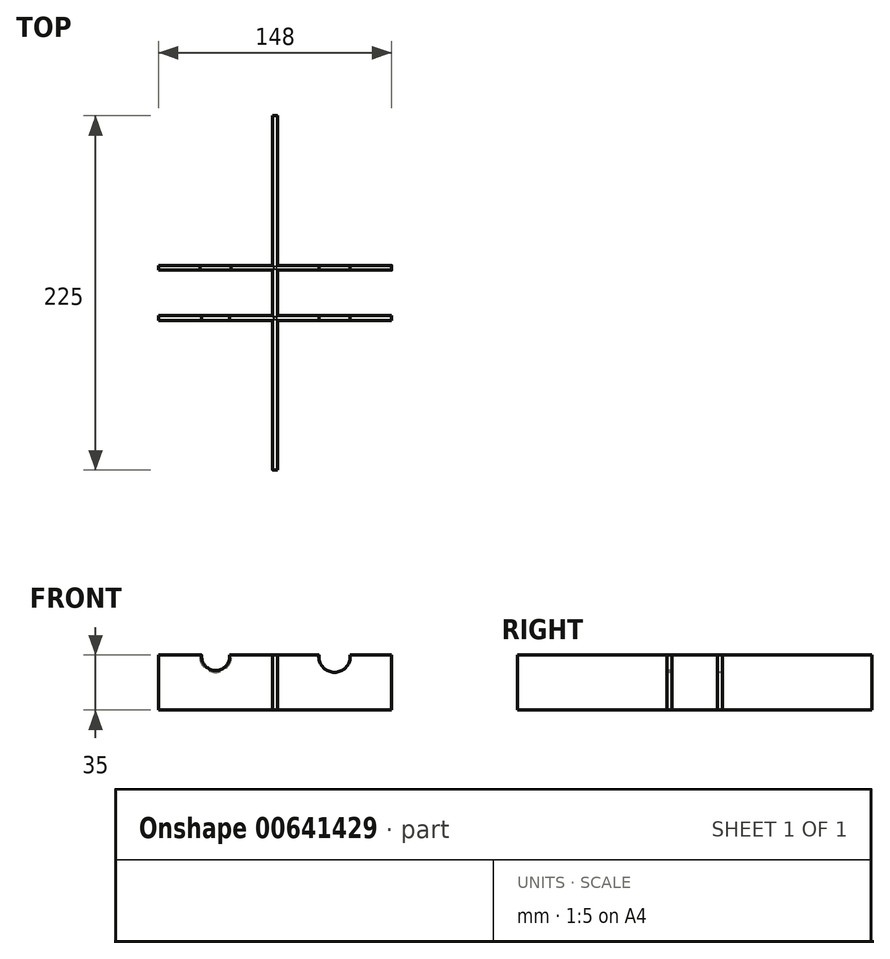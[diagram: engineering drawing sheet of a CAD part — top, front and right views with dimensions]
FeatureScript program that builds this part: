
annotation { "Feature Type Name" : "Feature", "Feature Type Description" : "" }
export const myFeature = defineFeature(function(context is Context, id is Id, definition is map)
    precondition{}
    {
        {
            var Q0;
            Q0=qCreatedBy(makeId("Top.planeOp"),FACE);
            var sketch = newSketch(context, id + "F0", { "sketchPlane" : qUnion([Q0])});
            skPoint(sketch, "E0.middle", {"position": v(0, 0) * mm});
            skLineSegment(sketch, "E1.bottom", {"start": v(1.5, 112.5) * mm, "end": v(-1.5, 112.5) * mm});
            skLineSegment(sketch, "E1.top", {"start": v(1.5, -112.5) * mm, "end": v(-1.5, -112.5) * mm});
            skLineSegment(sketch, "E2", {"start": v(-1.5, -17.5) * mm, "end": v(-74, -17.5) * mm});
            skLineSegment(sketch, "E3", {"start": v(-74, -17.5) * mm, "end": v(-74, -14.5) * mm});
            skLineSegment(sketch, "E4", {"start": v(-74, -14.5) * mm, "end": v(-1.5, -14.5) * mm});
            skLineSegment(sketch, "E5", {"start": v(1.5, -17.5) * mm, "end": v(74, -17.5) * mm});
            skLineSegment(sketch, "E6", {"start": v(74, -17.5) * mm, "end": v(74, -14.5) * mm});
            skLineSegment(sketch, "E7", {"start": v(74, -14.5) * mm, "end": v(1.5, -14.5) * mm});
            skLineSegment(sketch, "E8", {"start": v(-1.5, 14.5) * mm, "end": v(-74, 14.5) * mm});
            skLineSegment(sketch, "E9", {"start": v(-74, 14.5) * mm, "end": v(-74, 17.5) * mm});
            skLineSegment(sketch, "E10", {"start": v(-74, 17.5) * mm, "end": v(-1.5, 17.5) * mm});
            skLineSegment(sketch, "E11", {"start": v(74, 17.5) * mm, "end": v(74, 14.5) * mm});
            skLineSegment(sketch, "E12", {"start": v(74, 17.5) * mm, "end": v(1.5, 17.5) * mm});
            skLineSegment(sketch, "E13", {"start": v(74, 14.5) * mm, "end": v(1.5, 14.5) * mm});
            skLineSegment(sketch, "E14", {"start": v(-1.5, 112.5) * mm, "end": v(-1.5, 17.5) * mm});
            skLineSegment(sketch, "E15", {"start": v(-1.5, 14.5) * mm, "end": v(-1.5, -14.5) * mm});
            skLineSegment(sketch, "E16", {"start": v(-1.5, -17.5) * mm, "end": v(-1.5, -112.5) * mm});
            skLineSegment(sketch, "E17", {"start": v(1.5, 112.5) * mm, "end": v(1.5, 17.5) * mm});
            skLineSegment(sketch, "E18", {"start": v(1.5, 14.5) * mm, "end": v(1.5, -14.5) * mm});
            skLineSegment(sketch, "E19", {"start": v(1.5, -17.5) * mm, "end": v(1.5, -112.5) * mm});
            skSolve(sketch);
        }
        {
            var Q0;
            Q0=makeQuery(id+"F0.imprint","IMPRINT",FACE,{"disambiguationData":[TD([[makeQuery(id+"F0.imprint","IMPRINT",EDGE,{"derivedFrom":sQuery(id+"F0.wireOp",EDGE,"E1.bottom")}),1.0]])]});
            extrude(context, id + "F1", {"entities" : qUnion([Q0]), "depth" : 35 * mm, "offsetDistance" : 25 * mm});
        }
        {
            var Q0;
            Q0=makeQuery(id+"F1.opExtrude","CAP_EDGE",EDGE,{"disambiguationData":[OSD([sQuery(id+"F0.wireOp",EDGE,"E8")])],"isStart":false});
            var Q1;
            Q1=makeQuery(id+"F1.opExtrude","CAP_EDGE",EDGE,{"disambiguationData":[OSD([sQuery(id+"F0.wireOp",EDGE,"E14")])],"isStart":false});
            var Q2;
            Q2=makeQuery(id+"F1.opExtrude","CAP_EDGE",EDGE,{"disambiguationData":[OSD([sQuery(id+"F0.wireOp",EDGE,"E10")])],"isStart":false});
            var Q3;
            Q3=makeQuery(id+"F1.opExtrude","CAP_EDGE",EDGE,{"disambiguationData":[OSD([sQuery(id+"F0.wireOp",EDGE,"E17")])],"isStart":false});
            var Q4;
            Q4=makeQuery(id+"F1.opExtrude","CAP_EDGE",EDGE,{"disambiguationData":[OSD([sQuery(id+"F0.wireOp",EDGE,"E12")])],"isStart":false});
            var Q5;
            Q5=makeQuery(id+"F1.opExtrude","CAP_EDGE",EDGE,{"disambiguationData":[OSD([sQuery(id+"F0.wireOp",EDGE,"E13")])],"isStart":false});
            var Q6;
            Q6=makeQuery(id+"F1.opExtrude","CAP_EDGE",EDGE,{"disambiguationData":[OSD([sQuery(id+"F0.wireOp",EDGE,"E18")])],"isStart":false});
            var Q7;
            Q7=makeQuery(id+"F1.opExtrude","CAP_EDGE",EDGE,{"disambiguationData":[OSD([sQuery(id+"F0.wireOp",EDGE,"E15")])],"isStart":false});
            var Q8;
            Q8=makeQuery(id+"F1.opExtrude","CAP_EDGE",EDGE,{"disambiguationData":[OSD([sQuery(id+"F0.wireOp",EDGE,"E4")])],"isStart":false});
            var Q9;
            Q9=makeQuery(id+"F1.opExtrude","CAP_EDGE",EDGE,{"disambiguationData":[OSD([sQuery(id+"F0.wireOp",EDGE,"E2")])],"isStart":false});
            var Q10;
            Q10=makeQuery(id+"F1.opExtrude","CAP_EDGE",EDGE,{"disambiguationData":[OSD([sQuery(id+"F0.wireOp",EDGE,"E7")])],"isStart":false});
            var Q11;
            Q11=makeQuery(id+"F1.opExtrude","CAP_EDGE",EDGE,{"disambiguationData":[OSD([sQuery(id+"F0.wireOp",EDGE,"E5")])],"isStart":false});
            var Q12;
            Q12=makeQuery(id+"F1.opExtrude","CAP_EDGE",EDGE,{"disambiguationData":[OSD([sQuery(id+"F0.wireOp",EDGE,"E16")])],"isStart":false});
            var Q13;
            Q13=makeQuery(id+"F1.opExtrude","CAP_EDGE",EDGE,{"disambiguationData":[OSD([sQuery(id+"F0.wireOp",EDGE,"E19")])],"isStart":false});
            fillet(context, id + "F2", {"entities" : qUnion([Q0, Q1, Q2, Q3, Q4, Q5, Q6, Q7, Q8, Q9, Q10, Q11, Q12, Q13]), "radius" : 1 * mm, "tangentPropagation" : true, "allowEdgeOverflow" : false});
        }
        {
            var Q0;
            Q0=makeQuery(id+"F1.opExtrude","SWEPT_FACE",FACE,{"disambiguationData":[OSD([sQuery(id+"F0.wireOp",EDGE,"E2")])]});
            var sketch = newSketch(context, id + "F3", { "sketchPlane" : qUnion([Q0])});
            skCircle(sketch, "E20", {"center": v(-37.75, 34) * mm, "radius": 8.88 * mm});
            skSolve(sketch);
        }
        {
            var Q0;
            {var subQ0=sQuery(id+"F3.wireOp",EDGE,"E20");var subQ1=sQuery(id+"F0.wireOp",EDGE,"E2");var subQ2=makeQuery(id+"F2.opFillet","BLEND_EDGE",EDGE,{"blendedFrom":[makeQuery(id+"F1.opExtrude","CAP_EDGE",EDGE,{"disambiguationData":[OSD([subQ1])],"isStart":false}),makeQuery(id+"F1.opExtrude","SWEPT_FACE",FACE,{"disambiguationData":[OSD([subQ1])]})],"blendedInto":[makeQuery(id+"F1.opExtrude","SWEPT_FACE",FACE,{"disambiguationData":[OSD([subQ1])]})]});var subQ3=makeQuery(id+"F3.imprint","INTERSECT",VERTEX,{"disambiguationData":[OD(0.0)],"derivedFrom":[subQ2,subQ0]});Q0=makeQuery(id+"F3.imprint","IMPRINT",FACE,{"disambiguationData":[TD([[makeQuery(id+"F3.imprint","IMPRINT",EDGE,{"disambiguationData":[TD([[subQ3,1.0]])],"derivedFrom":subQ0}),1.0]])]});}
            var Q1;
            {var subQ0=sQuery(id+"F3.wireOp",EDGE,"E20");var subQ1=sQuery(id+"F0.wireOp",EDGE,"E2");var subQ2=makeQuery(id+"F2.opFillet","BLEND_EDGE",EDGE,{"blendedFrom":[makeQuery(id+"F1.opExtrude","CAP_EDGE",EDGE,{"disambiguationData":[OSD([subQ1])],"isStart":false}),makeQuery(id+"F1.opExtrude","SWEPT_FACE",FACE,{"disambiguationData":[OSD([subQ1])]})],"blendedInto":[makeQuery(id+"F1.opExtrude","SWEPT_FACE",FACE,{"disambiguationData":[OSD([subQ1])]})]});var subQ3=makeQuery(id+"F3.imprint","INTERSECT",VERTEX,{"disambiguationData":[OD(0.0)],"derivedFrom":[subQ2,subQ0]});Q1=makeQuery(id+"F3.imprint","IMPRINT",FACE,{"disambiguationData":[TD([[makeQuery(id+"F3.imprint","IMPRINT",EDGE,{"disambiguationData":[TD([[subQ3,-1.0]])],"derivedFrom":subQ0}),1.0]])]});}
            extrude(context, id + "F4", {"entities" : qUnion([Q0, Q1]), "operationType" : NewBodyOperationType.REMOVE, "oppositeDirection" : true, "depth" : 25 * mm, "offsetDistance" : 25 * mm});
        }
        {
            var Q0;
            Q0=makeQuery(id+"F1.opExtrude","SWEPT_FACE",FACE,{"disambiguationData":[OSD([sQuery(id+"F0.wireOp",EDGE,"E8")])]});
            var sketch = newSketch(context, id + "F5", { "sketchPlane" : qUnion([Q0])});
            skCircle(sketch, "E21", {"center": v(-37.75, 34) * mm, "radius": 10 * mm});
            skSolve(sketch);
        }
        {
            var Q0;
            {var subQ0=sQuery(id+"F5.wireOp",EDGE,"E21");var subQ1=sQuery(id+"F0.wireOp",EDGE,"E8");var subQ2=makeQuery(id+"F2.opFillet","BLEND_EDGE",EDGE,{"blendedFrom":[makeQuery(id+"F1.opExtrude","CAP_EDGE",EDGE,{"disambiguationData":[OSD([subQ1])],"isStart":false}),makeQuery(id+"F1.opExtrude","SWEPT_FACE",FACE,{"disambiguationData":[OSD([subQ1])]})],"blendedInto":[makeQuery(id+"F1.opExtrude","SWEPT_FACE",FACE,{"disambiguationData":[OSD([subQ1])]})]});var subQ3=makeQuery(id+"F5.imprint","INTERSECT",VERTEX,{"disambiguationData":[OD(0.0)],"derivedFrom":[subQ2,subQ0]});Q0=makeQuery(id+"F5.imprint","IMPRINT",FACE,{"disambiguationData":[TD([[makeQuery(id+"F5.imprint","IMPRINT",EDGE,{"disambiguationData":[TD([[subQ3,1.0]])],"derivedFrom":subQ0}),1.0]])]});}
            var Q1;
            {var subQ0=sQuery(id+"F5.wireOp",EDGE,"E21");var subQ1=sQuery(id+"F0.wireOp",EDGE,"E8");var subQ2=makeQuery(id+"F2.opFillet","BLEND_EDGE",EDGE,{"blendedFrom":[makeQuery(id+"F1.opExtrude","CAP_EDGE",EDGE,{"disambiguationData":[OSD([subQ1])],"isStart":false}),makeQuery(id+"F1.opExtrude","SWEPT_FACE",FACE,{"disambiguationData":[OSD([subQ1])]})],"blendedInto":[makeQuery(id+"F1.opExtrude","SWEPT_FACE",FACE,{"disambiguationData":[OSD([subQ1])]})]});var subQ3=makeQuery(id+"F5.imprint","INTERSECT",VERTEX,{"disambiguationData":[OD(0.0)],"derivedFrom":[subQ2,subQ0]});Q1=makeQuery(id+"F5.imprint","IMPRINT",FACE,{"disambiguationData":[TD([[makeQuery(id+"F5.imprint","IMPRINT",EDGE,{"disambiguationData":[TD([[subQ3,-1.0]])],"derivedFrom":subQ0}),1.0]])]});}
            extrude(context, id + "F6", {"entities" : qUnion([Q0, Q1]), "operationType" : NewBodyOperationType.REMOVE, "oppositeDirection" : true, "depth" : 25 * mm, "offsetDistance" : 25 * mm});
        }
        {
            var Q0;
            Q0=makeQuery(id+"F1.opExtrude","SWEPT_FACE",FACE,{"disambiguationData":[OSD([sQuery(id+"F0.wireOp",EDGE,"E5")])]});
            var sketch = newSketch(context, id + "F7", { "sketchPlane" : qUnion([Q0])});
            skCircle(sketch, "E22", {"center": v(37.75, 34) * mm, "radius": 10 * mm});
            skSolve(sketch);
        }
        {
            var Q0;
            {var subQ0=sQuery(id+"F7.wireOp",EDGE,"E22");var subQ1=sQuery(id+"F0.wireOp",EDGE,"E5");var subQ2=makeQuery(id+"F2.opFillet","BLEND_EDGE",EDGE,{"blendedFrom":[makeQuery(id+"F1.opExtrude","CAP_EDGE",EDGE,{"disambiguationData":[OSD([subQ1])],"isStart":false}),makeQuery(id+"F1.opExtrude","SWEPT_FACE",FACE,{"disambiguationData":[OSD([subQ1])]})],"blendedInto":[makeQuery(id+"F1.opExtrude","SWEPT_FACE",FACE,{"disambiguationData":[OSD([subQ1])]})]});var subQ3=makeQuery(id+"F7.imprint","INTERSECT",VERTEX,{"disambiguationData":[OD(0.0)],"derivedFrom":[subQ2,subQ0]});Q0=makeQuery(id+"F7.imprint","IMPRINT",FACE,{"disambiguationData":[TD([[makeQuery(id+"F7.imprint","IMPRINT",EDGE,{"disambiguationData":[TD([[subQ3,-1.0]])],"derivedFrom":subQ0}),1.0]])]});}
            var Q1;
            {var subQ0=sQuery(id+"F7.wireOp",EDGE,"E22");var subQ1=sQuery(id+"F0.wireOp",EDGE,"E5");var subQ2=makeQuery(id+"F2.opFillet","BLEND_EDGE",EDGE,{"blendedFrom":[makeQuery(id+"F1.opExtrude","CAP_EDGE",EDGE,{"disambiguationData":[OSD([subQ1])],"isStart":false}),makeQuery(id+"F1.opExtrude","SWEPT_FACE",FACE,{"disambiguationData":[OSD([subQ1])]})],"blendedInto":[makeQuery(id+"F1.opExtrude","SWEPT_FACE",FACE,{"disambiguationData":[OSD([subQ1])]})]});var subQ3=makeQuery(id+"F7.imprint","INTERSECT",VERTEX,{"disambiguationData":[OD(0.0)],"derivedFrom":[subQ2,subQ0]});Q1=makeQuery(id+"F7.imprint","IMPRINT",FACE,{"disambiguationData":[TD([[makeQuery(id+"F7.imprint","IMPRINT",EDGE,{"disambiguationData":[TD([[subQ3,1.0]])],"derivedFrom":subQ0}),1.0]])]});}
            extrude(context, id + "F8", {"entities" : qUnion([Q0, Q1]), "operationType" : NewBodyOperationType.REMOVE, "oppositeDirection" : true, "depth" : 25 * mm, "offsetDistance" : 25 * mm});
        }
        {
            var Q0;
            Q0=makeQuery(id+"F1.opExtrude","SWEPT_FACE",FACE,{"disambiguationData":[OSD([sQuery(id+"F0.wireOp",EDGE,"E13")])]});
            var sketch = newSketch(context, id + "F9", { "sketchPlane" : qUnion([Q0])});
            skCircle(sketch, "E23", {"center": v(37.75, 34) * mm, "radius": 10 * mm});
            skSolve(sketch);
        }
        {
            var Q0;
            {var subQ0=sQuery(id+"F9.wireOp",EDGE,"E23");var subQ1=sQuery(id+"F0.wireOp",EDGE,"E13");var subQ2=makeQuery(id+"F2.opFillet","BLEND_EDGE",EDGE,{"blendedFrom":[makeQuery(id+"F1.opExtrude","CAP_EDGE",EDGE,{"disambiguationData":[OSD([subQ1])],"isStart":false}),makeQuery(id+"F1.opExtrude","SWEPT_FACE",FACE,{"disambiguationData":[OSD([subQ1])]})],"blendedInto":[makeQuery(id+"F1.opExtrude","SWEPT_FACE",FACE,{"disambiguationData":[OSD([subQ1])]})]});var subQ3=makeQuery(id+"F9.imprint","INTERSECT",VERTEX,{"disambiguationData":[OD(0.0)],"derivedFrom":[subQ2,subQ0]});Q0=makeQuery(id+"F9.imprint","IMPRINT",FACE,{"disambiguationData":[TD([[makeQuery(id+"F9.imprint","IMPRINT",EDGE,{"disambiguationData":[TD([[subQ3,-1.0]])],"derivedFrom":subQ0}),1.0]])]});}
            var Q1;
            {var subQ0=sQuery(id+"F9.wireOp",EDGE,"E23");var subQ1=sQuery(id+"F0.wireOp",EDGE,"E13");var subQ2=makeQuery(id+"F2.opFillet","BLEND_EDGE",EDGE,{"blendedFrom":[makeQuery(id+"F1.opExtrude","CAP_EDGE",EDGE,{"disambiguationData":[OSD([subQ1])],"isStart":false}),makeQuery(id+"F1.opExtrude","SWEPT_FACE",FACE,{"disambiguationData":[OSD([subQ1])]})],"blendedInto":[makeQuery(id+"F1.opExtrude","SWEPT_FACE",FACE,{"disambiguationData":[OSD([subQ1])]})]});var subQ3=makeQuery(id+"F9.imprint","INTERSECT",VERTEX,{"disambiguationData":[OD(0.0)],"derivedFrom":[subQ2,subQ0]});Q1=makeQuery(id+"F9.imprint","IMPRINT",FACE,{"disambiguationData":[TD([[makeQuery(id+"F9.imprint","IMPRINT",EDGE,{"disambiguationData":[TD([[subQ3,1.0]])],"derivedFrom":subQ0}),1.0]])]});}
            extrude(context, id + "F10", {"entities" : qUnion([Q0, Q1]), "operationType" : NewBodyOperationType.REMOVE, "oppositeDirection" : true, "depth" : 25 * mm, "offsetDistance" : 25 * mm});
        }
    });
